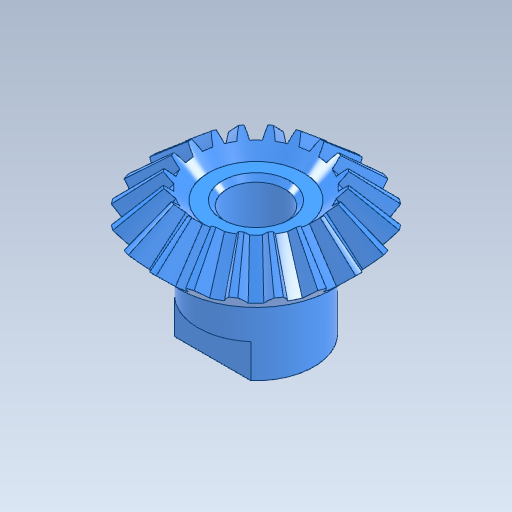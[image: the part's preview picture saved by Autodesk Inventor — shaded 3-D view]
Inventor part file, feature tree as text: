
AUTODESK INVENTOR PART (.ipt)
format: ipt  version: 2024 (Build 280153000, 153)  size: 429,568 bytes
history: native  units: mm
features: other x5, sketch x2, revolve x1, extrude x1
ambient origin geometry x8: Origin, YZ Plane, XZ Plane, XY Plane, X Axis, Y Axis, Z Axis, Center Point
bodies: Solid1 (feature_tree)
feature tree (9):
  other  "_PM1-20.ipt"
  sketch  "スケッチ1"
  sketch  "スケッチ2"
  revolve  "回転1"
  extrude  "押し出し1"  Depth=10.0mm
  other  "厚み1"
  other  "厚み2"
  other  "Solid1::_PM1-20.ipt"
  other  "TaggingFeature1"
